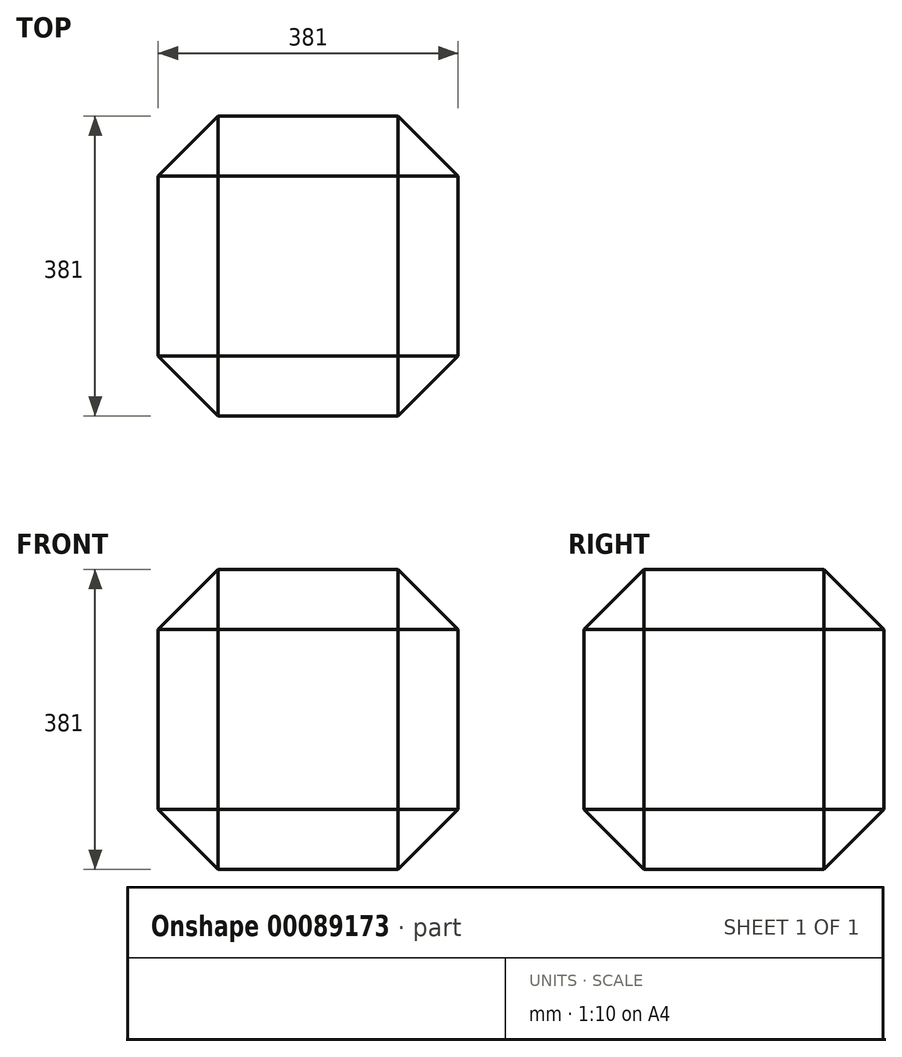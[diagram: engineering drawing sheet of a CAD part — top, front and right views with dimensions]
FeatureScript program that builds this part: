
annotation { "Feature Type Name" : "Feature", "Feature Type Description" : "" }
export const myFeature = defineFeature(function(context is Context, id is Id, definition is map)
    precondition{}
    {
        {
            var Q0;
            Q0=qCreatedBy(makeId("Front.planeOp"),FACE);
            var sketch = newSketch(context, id + "F0", { "sketchPlane" : qUnion([Q0])});
            skLineSegment(sketch, "E0.bottom", {"start": v(0, 0) * mm, "end": v(381, 0) * mm});
            skLineSegment(sketch, "E0.top", {"start": v(0, -381) * mm, "end": v(381, -381) * mm});
            skLineSegment(sketch, "E0.left", {"start": v(0, 0) * mm, "end": v(0, -381) * mm});
            skLineSegment(sketch, "E0.right", {"start": v(381, 0) * mm, "end": v(381, -381) * mm});
            skSolve(sketch);
        }
        {
            var Q0;
            Q0 = qSketchRegion(id + "F0", true);
            extrude(context, id + "F1", {"entities" : qUnion([Q0]), "depth" : 381 * mm});
        }
        {
            var Q0;
            Q0=makeQuery(id+"F1.opExtrude","SWEPT_EDGE",EDGE,{"disambiguationData":[OSD([sQuery(id+"F0.wireOp",EDGE,"E0.bottom"),sQuery(id+"F0.wireOp",EDGE,"E0.right")])]});
            var Q1;
            Q1=makeQuery(id+"F1.opExtrude","CAP_EDGE",EDGE,{"disambiguationData":[OSD([sQuery(id+"F0.wireOp",EDGE,"E0.bottom")])],"isStart":false});
            var Q2;
            Q2=makeQuery(id+"F1.opExtrude","SWEPT_EDGE",EDGE,{"disambiguationData":[OSD([sQuery(id+"F0.wireOp",EDGE,"E0.bottom"),sQuery(id+"F0.wireOp",EDGE,"E0.left")])]});
            var Q3;
            Q3=makeQuery(id+"F1.opExtrude","CAP_EDGE",EDGE,{"disambiguationData":[OSD([sQuery(id+"F0.wireOp",EDGE,"E0.bottom")])],"isStart":true});
            var Q4;
            Q4=makeQuery(id+"F1.opExtrude","CAP_EDGE",EDGE,{"disambiguationData":[OSD([sQuery(id+"F0.wireOp",EDGE,"E0.right")])],"isStart":true});
            var Q5;
            Q5=makeQuery(id+"F1.opExtrude","CAP_EDGE",EDGE,{"disambiguationData":[OSD([sQuery(id+"F0.wireOp",EDGE,"E0.right")])],"isStart":false});
            var Q6;
            Q6=makeQuery(id+"F1.opExtrude","CAP_EDGE",EDGE,{"disambiguationData":[OSD([sQuery(id+"F0.wireOp",EDGE,"E0.left")])],"isStart":false});
            var Q7;
            Q7=makeQuery(id+"F1.opExtrude","SWEPT_EDGE",EDGE,{"disambiguationData":[OSD([sQuery(id+"F0.wireOp",EDGE,"E0.top"),sQuery(id+"F0.wireOp",EDGE,"E0.left")])]});
            var Q8;
            Q8=makeQuery(id+"F1.opExtrude","CAP_EDGE",EDGE,{"disambiguationData":[OSD([sQuery(id+"F0.wireOp",EDGE,"E0.top")])],"isStart":false});
            var Q9;
            Q9=makeQuery(id+"F1.opExtrude","SWEPT_EDGE",EDGE,{"disambiguationData":[OSD([sQuery(id+"F0.wireOp",EDGE,"E0.top"),sQuery(id+"F0.wireOp",EDGE,"E0.right")])]});
            var Q10;
            Q10=makeQuery(id+"F1.opExtrude","CAP_EDGE",EDGE,{"disambiguationData":[OSD([sQuery(id+"F0.wireOp",EDGE,"E0.top")])],"isStart":true});
            var Q11;
            Q11=makeQuery(id+"F1.opExtrude","CAP_EDGE",EDGE,{"disambiguationData":[OSD([sQuery(id+"F0.wireOp",EDGE,"E0.left")])],"isStart":true});
            chamfer(context, id + "F2", {"entities" : qUnion([Q0, Q1, Q2, Q3, Q4, Q5, Q6, Q7, Q8, Q9, Q10, Q11]), "width" : 76.2 * mm, "tangentPropagation" : true});
        }
    });
